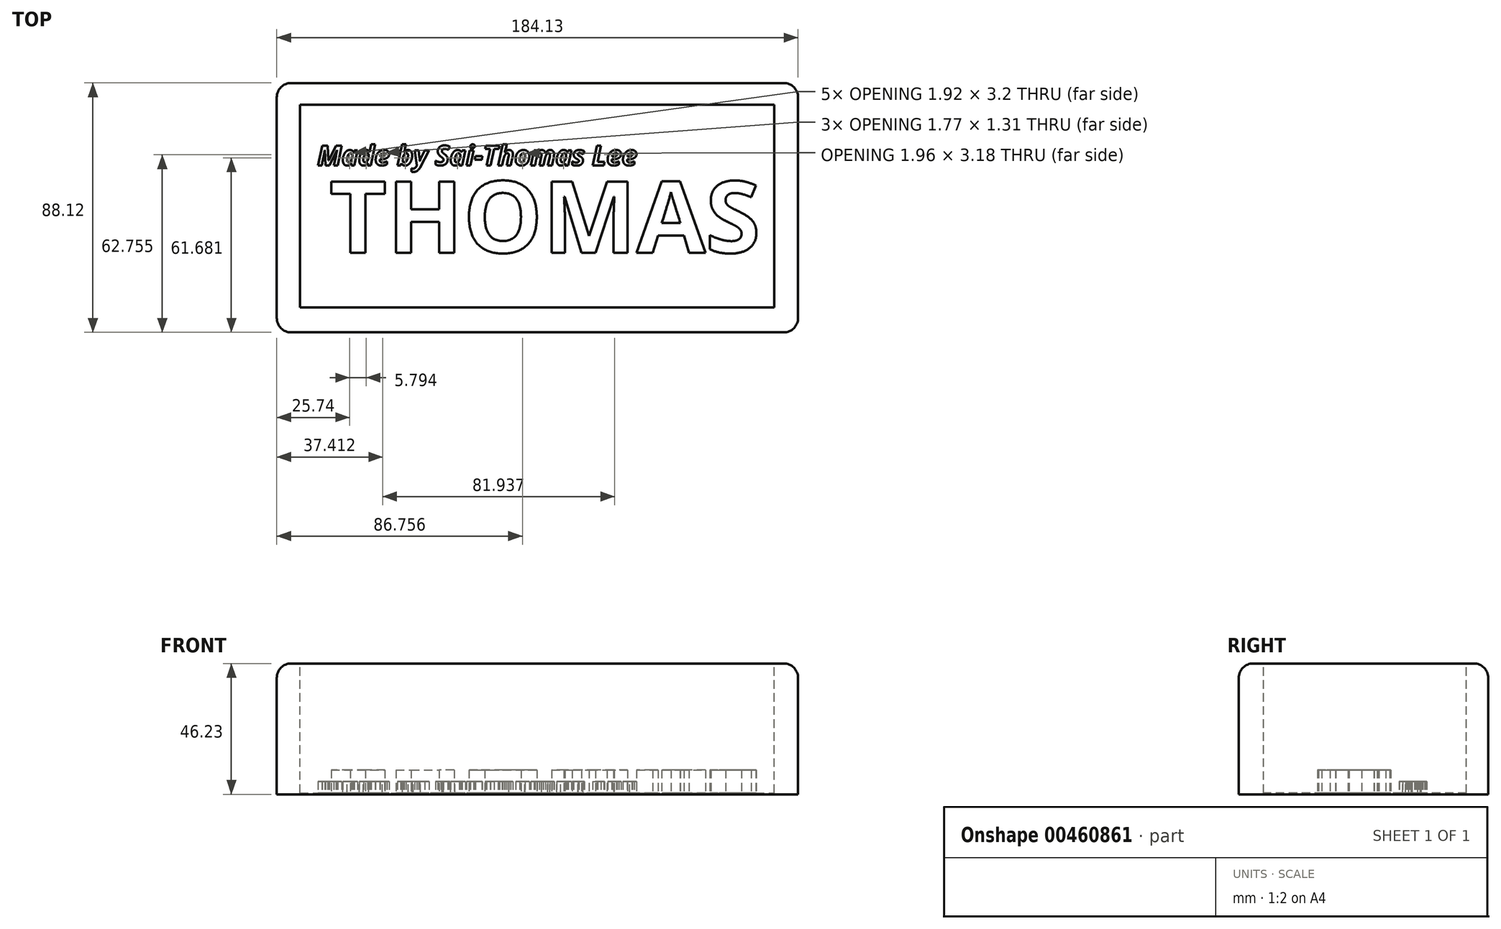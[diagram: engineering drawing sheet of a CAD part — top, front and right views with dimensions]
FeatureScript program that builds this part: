
annotation { "Feature Type Name" : "Feature", "Feature Type Description" : "" }
export const myFeature = defineFeature(function(context is Context, id is Id, definition is map)
    precondition{}
    {
        {
            var Q0;
            Q0=qCreatedBy(makeId("Top.planeOp"),FACE);
            var sketch = newSketch(context, id + "F0", { "sketchPlane" : qUnion([Q0])});
            skLineSegment(sketch, "E0.bottom", {"start": v(-90.86, 44.5) * mm, "end": v(93.27, 44.5) * mm});
            skLineSegment(sketch, "E0.top", {"start": v(-90.86, -43.62) * mm, "end": v(93.27, -43.62) * mm});
            skLineSegment(sketch, "E0.left", {"start": v(-90.86, 44.5) * mm, "end": v(-90.86, -43.62) * mm});
            skLineSegment(sketch, "E0.right", {"start": v(93.27, 44.5) * mm, "end": v(93.27, -43.62) * mm});
            skSolve(sketch);
        }
        {
            var Q0;
            Q0 = qSketchRegion(id + "F0", true);
            extrude(context, id + "F1", {"entities" : qUnion([Q0]), "depth" : 46.23 * mm});
        }
        {
            var Q0;
            Q0=makeQuery(id+"F1.opExtrude","CAP_EDGE",EDGE,{"disambiguationData":[OSD([sQuery(id+"F0.wireOp",EDGE,"E0.left")])],"isStart":false});
            var Q1;
            Q1=makeQuery(id+"F1.opExtrude","CAP_EDGE",EDGE,{"disambiguationData":[OSD([sQuery(id+"F0.wireOp",EDGE,"E0.top")])],"isStart":false});
            var Q2;
            Q2=makeQuery(id+"F1.opExtrude","SWEPT_EDGE",EDGE,{"disambiguationData":[OSD([sQuery(id+"F0.wireOp",EDGE,"E0.top"),sQuery(id+"F0.wireOp",EDGE,"E0.left")])]});
            var Q3;
            Q3=makeQuery(id+"F1.opExtrude","SWEPT_EDGE",EDGE,{"disambiguationData":[OSD([sQuery(id+"F0.wireOp",EDGE,"E0.top"),sQuery(id+"F0.wireOp",EDGE,"E0.right")])]});
            var Q4;
            Q4=makeQuery(id+"F1.opExtrude","CAP_EDGE",EDGE,{"disambiguationData":[OSD([sQuery(id+"F0.wireOp",EDGE,"E0.right")])],"isStart":false});
            var Q5;
            Q5=makeQuery(id+"F1.opExtrude","SWEPT_EDGE",EDGE,{"disambiguationData":[OSD([sQuery(id+"F0.wireOp",EDGE,"E0.bottom"),sQuery(id+"F0.wireOp",EDGE,"E0.right")])]});
            var Q6;
            Q6=makeQuery(id+"F1.opExtrude","CAP_EDGE",EDGE,{"disambiguationData":[OSD([sQuery(id+"F0.wireOp",EDGE,"E0.bottom")])],"isStart":false});
            var Q7;
            Q7=makeQuery(id+"F1.opExtrude","SWEPT_EDGE",EDGE,{"disambiguationData":[OSD([sQuery(id+"F0.wireOp",EDGE,"E0.bottom"),sQuery(id+"F0.wireOp",EDGE,"E0.left")])]});
            fillet(context, id + "F2", {"entities" : qUnion([Q0, Q1, Q2, Q3, Q4, Q5, Q6, Q7]), "radius" : 5.08 * mm, "tangentPropagation" : true, "allowEdgeOverflow" : false});
        }
        {
            var Q0;
            Q0=makeQuery(id+"F1.opExtrude","CAP_FACE",FACE,{"disambiguationData":[OSD([sQuery(id+"F0.wireOp",EDGE,"E0.bottom"),sQuery(id+"F0.wireOp",EDGE,"E0.top"),sQuery(id+"F0.wireOp",EDGE,"E0.left"),sQuery(id+"F0.wireOp",EDGE,"E0.right")])],"isStart":false});
            var sketch = newSketch(context, id + "F3", { "sketchPlane" : qUnion([Q0])});
            skLineSegment(sketch, "E1.bottom", {"start": v(-82.69, 36.8) * mm, "end": v(84.84, 36.8) * mm});
            skLineSegment(sketch, "E1.top", {"start": v(-82.69, -34.82) * mm, "end": v(84.84, -34.82) * mm});
            skLineSegment(sketch, "E1.left", {"start": v(-82.69, 36.8) * mm, "end": v(-82.69, -34.82) * mm});
            skLineSegment(sketch, "E1.right", {"start": v(84.84, 36.8) * mm, "end": v(84.84, -34.82) * mm});
            skSolve(sketch);
        }
        {
            var Q0;
            Q0 = qSketchRegion(id + "F3", true);
            extrude(context, id + "F4", {"entities" : qUnion([Q0]), "operationType" : NewBodyOperationType.REMOVE, "oppositeDirection" : true, "depth" : 45.72 * mm});
        }
        {
            var Q0;
            Q0=makeQuery(id+"F4.boolean.opBoolean","COPY",FACE,{"derivedFrom":makeQuery(id+"F4.opExtrude","CAP_FACE",FACE,{"disambiguationData":[OSD([sQuery(id+"F3.wireOp",EDGE,"E1.bottom"),sQuery(id+"F3.wireOp",EDGE,"E1.top"),sQuery(id+"F3.wireOp",EDGE,"E1.left"),sQuery(id+"F3.wireOp",EDGE,"E1.right")])],"isStart":false})});
            var sketch = newSketch(context, id + "F5", { "sketchPlane" : qUnion([Q0])});
            skText(sketch, "E2", { "text": "THOMAS", "fontName": "OpenSans-Bold.ttf"});
            const initialGuessF5  = {"E2": [-0.07236, -0.01545, 1, 0, 0.02536]};
            skSetInitialGuess(sketch, initialGuessF5);
            skSolve(sketch);
        }
        {
            var Q0;
            Q0 = qSketchRegion(id + "F5", true);
            extrude(context, id + "F6", {"entities" : qUnion([Q0]), "operationType" : NewBodyOperationType.ADD, "depth" : 8.13 * mm});
        }
        {
            var Q0;
            {var subQ0=sQuery(id+"F3.wireOp",EDGE,"E1.right");var subQ1=sQuery(id+"F3.wireOp",EDGE,"E1.bottom");var subQ2=sQuery(id+"F3.wireOp",EDGE,"E1.top");var subQ3=sQuery(id+"F3.wireOp",EDGE,"E1.left");Q0=makeQuery(id+"F6.boolean.opBoolean","SPLIT",FACE,{"disambiguationData":[TD([makeQuery(id+"F4.boolean.opBoolean","COPY",FACE,{"derivedFrom":makeQuery(id+"F4.opExtrude","SWEPT_FACE",FACE,{"disambiguationData":[OSD([subQ1])]})})])],"derivedFrom":makeQuery(id+"F4.boolean.opBoolean","COPY",FACE,{"derivedFrom":makeQuery(id+"F4.opExtrude","CAP_FACE",FACE,{"disambiguationData":[OSD([subQ1,subQ2,subQ3,subQ0])],"isStart":false})})});}
            var sketch = newSketch(context, id + "F7", { "sketchPlane" : qUnion([Q0])});
            skText(sketch, "E3", { "text": "Made by Sai-Thomas Lee", "fontName": "OpenSans-BoldItalic.ttf"});
            const initialGuessF7  = {"E3": [-0.07654, 0.0154, 1, 0, 0.00702]};
            skSetInitialGuess(sketch, initialGuessF7);
            skSolve(sketch);
        }
        {
            var Q0;
            Q0 = qSketchRegion(id + "F7", true);
            extrude(context, id + "F8", {"entities" : qUnion([Q0]), "depth" : 4.06 * mm});
        }
    });
